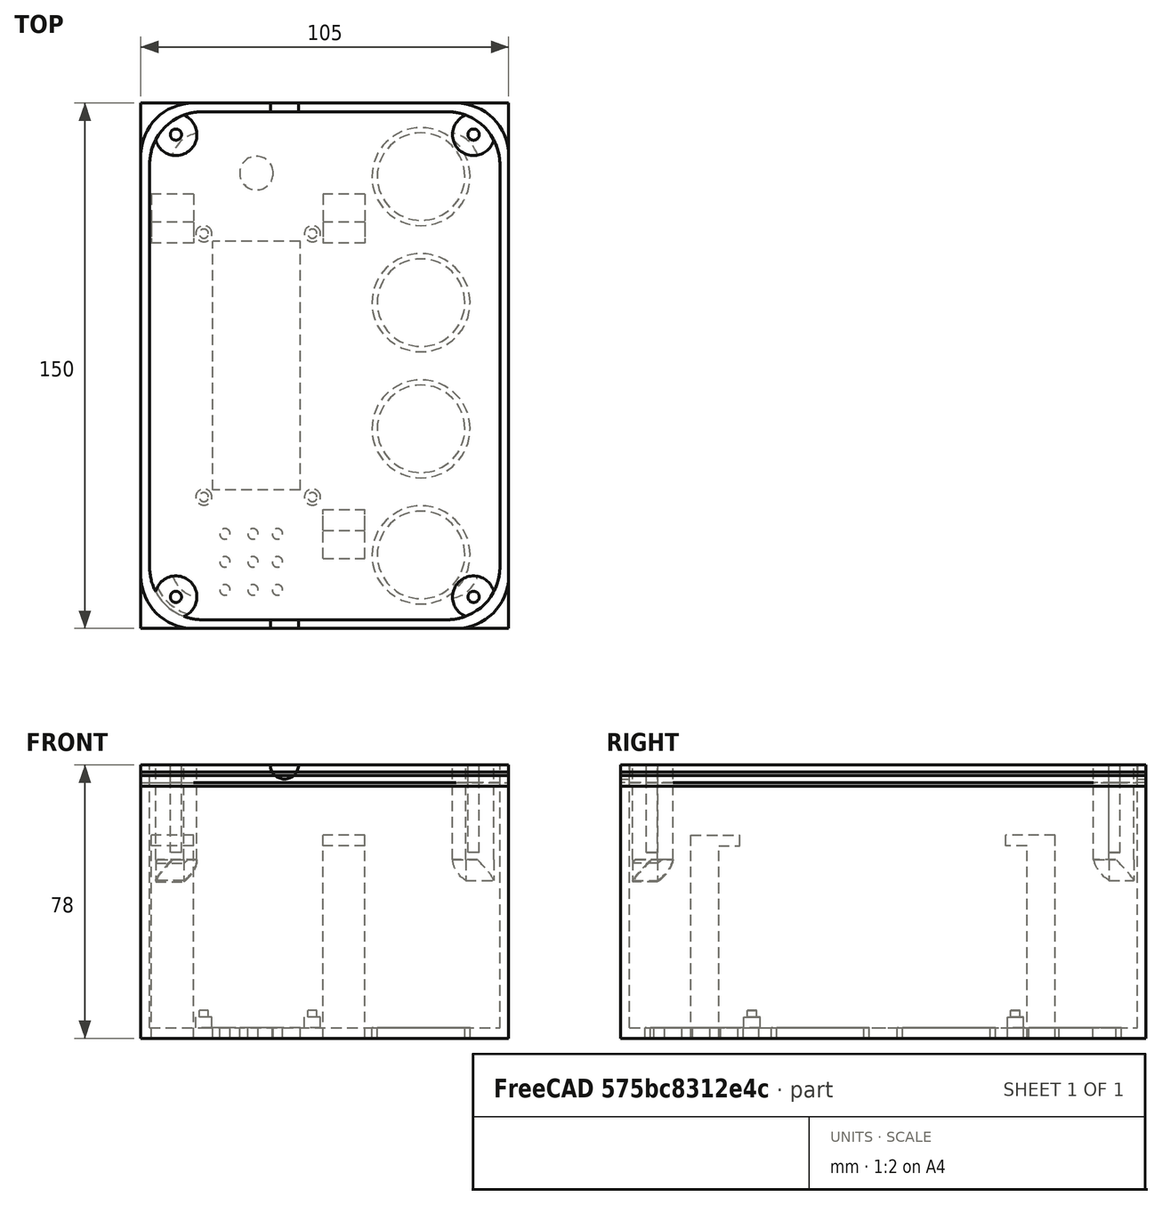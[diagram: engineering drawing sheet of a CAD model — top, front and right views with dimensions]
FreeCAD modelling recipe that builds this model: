
FCSTD DOCUMENT  (FreeCAD 0.16R6706 (Git))
Label: Simon_v2
License: All rights reserved
LicenseURL: http://en.wikipedia.org/wiki/All_rights_reserved
objects: Part::Cylinder×29, Part::Box×13, Part::Cut×13, Part::MultiFuse×11, Part::FeaturePython×6, Part::Fillet×5, Part::Chamfer×5, Mesh::Feature×1, Part::Fuse×1
note: 83 computed .brp shape members not serialized (recipe doc carries the construction recipe); baked Part::Feature solids carry a one-line shape summary decoded from their .brp

FEATURE [Part::Box] Box  label="Cubo"
  Height = 78
  Length = 105
  Width = 150
FEATURE [Part::Box] Box001  label="Cubo001"
  Height = 75
  Length = 100
  Placement = pos=(2.5,2.5,3) rot=(0,0,1;0rad)
  Width = 145
FEATURE [Part::Cut] Cut  label="caja"
  Base = -> Box
  Tool = -> Box001
FEATURE [Part::Cylinder] Cylinder  label="Cilindro"
  Angle = 360
  Height = 10
  Placement = pos=(80,25,0) rot=(0,0,1;0rad)
  Radius = 14
FEATURE [Part::FeaturePython] Array  label="Botones"  # Draft array (typed FeaturePython)
  Angle = 360
  ArrayType = 0
  Axis = (0,0,1)
  Base = -> Cylinder
  Center = (0,0,0)
  Fuse = false
  IntervalAxis = (0,0,0)
  IntervalX = (1,0,0)
  IntervalY = (0,36,0)
  IntervalZ = (0,0,1)
  NumberPolar = 1
  NumberX = 1
  NumberY = 4
  NumberZ = 1
  Placement = pos=(0,-4,-2) rot=(0,0,1;0rad)
FEATURE [Part::Cut] Cut001
  Base = -> Cut
  Tool = -> Array
FEATURE [Part::Box] Box002  label="Cubo002"
  Height = 10
  Length = 25
  Placement = pos=(20.5,39.5,-1) rot=(0,0,1;0rad)
  Width = 71
FEATURE [Part::Cut] Cut002
  Base = -> Cut001
  Tool = -> Box002
FEATURE [Part::Fillet] Fillet
  Base = -> Cut002
  Edges = 4 edges r=15: [Edge25,Edge26,Edge29,Edge30]
FEATURE [Part::Fillet] Fillet001
  Base = -> Fillet
  Edges = 4 edges r=15: [Edge29,Edge30,Edge33,Edge35]
FEATURE [Mesh::Feature] LCD
  Placement = pos=(15.5,35,8) rot=(0.707107,0.707107,0;3.14159rad)
FEATURE [Part::Cylinder] Cylinder001  label="Cilindro001"
  Angle = 360
  Height = 5
  Placement = pos=(18,37.5,3) rot=(0,0,1;0rad)
  Radius = 1.3
FEATURE [Part::FeaturePython] Array001  # Draft array (typed FeaturePython)
  Angle = 360
  ArrayType = 0
  Axis = (0,0,1)
  Base = -> Cylinder001
  Center = (0,0,0)
  Fuse = false
  IntervalAxis = (0,0,0)
  IntervalX = (31,0,0)
  IntervalY = (0,75.2,0)
  IntervalZ = (0,0,1)
  NumberPolar = 1
  NumberX = 2
  NumberY = 2
  NumberZ = 1
FEATURE [Part::Cylinder] Cylinder002  label="Cilindro002"
  Angle = 360
  Height = 3
  Placement = pos=(18,37.5,3) rot=(0,0,1;0rad)
  Radius = 2.3
FEATURE [Part::FeaturePython] Array002  # Draft array (typed FeaturePython)
  Angle = 360
  ArrayType = 0
  Axis = (0,0,1)
  Base = -> Cylinder002
  Center = (0,0,0)
  Fuse = false
  IntervalAxis = (0,0,0)
  IntervalX = (31,0,0)
  IntervalY = (0,75.2,0)
  IntervalZ = (0,0,1)
  NumberPolar = 1
  NumberX = 2
  NumberY = 2
  NumberZ = 1
FEATURE [Part::Fuse] Fusion
  Base = -> Array001
  Tool = -> Array002
FEATURE [Part::MultiFuse] Fusion001
  Shapes = -> [Fillet001,Fusion]
FEATURE [Part::Cylinder] Cylinder003  label="Cilindro003"
  Angle = 360
  Height = 27
  Placement = pos=(10,9,51) rot=(0,0,1;0rad)
  Radius = 6
FEATURE [Part::MultiFuse] Fusion002
  Shapes = -> [Fusion001,Cylinder003]
FEATURE [Part::Chamfer] Chamfer
  Base = -> Fusion002
  Edges = 1 edges r=6.3: [Edge8]
FEATURE [Part::Chamfer] Chamfer001
  Base = -> Fusion002
  Edges = 1 edges r=1: [Edge8]
FEATURE [Part::Cylinder] Cylinder004  label="Cilindro004"
  Angle = 360
  Height = 27
  Placement = pos=(95,9,51) rot=(0,0,1;0rad)
  Radius = 6
FEATURE [Part::Cylinder] Cylinder005  label="Cilindro005"
  Angle = 360
  Height = 27
  Placement = pos=(95,141,51) rot=(0,0,1;0rad)
  Radius = 6
FEATURE [Part::Cylinder] Cylinder007  label="Cilindro007"
  Angle = 360
  Height = 27
  Placement = pos=(10,141,51) rot=(0,0,1;0rad)
  Radius = 6
FEATURE [Part::MultiFuse] Fusion003
  Shapes = -> [Cylinder004,Cylinder005,Cylinder007]
FEATURE [Part::MultiFuse] Fusion004
  Shapes = -> [Chamfer,Fusion003]
FEATURE [Part::Chamfer] Chamfer002
  Base = -> Fusion004
  Edges = 1 edges r=6: [Edge94]
FEATURE [Part::Chamfer] Chamfer003
  Base = -> Chamfer002
  Edges = 1 edges r=6: [Edge96]
FEATURE [Part::Chamfer] Chamfer004
  Base = -> Chamfer003
  Edges = 1 edges r=6: [Edge88]
FEATURE [Part::Cylinder] Cylinder008  label="Cilindro008"
  Angle = 360
  Height = 28
  Placement = pos=(10,141,51) rot=(0,0,1;0rad)
  Radius = 1.6
FEATURE [Part::Cylinder] Cylinder009  label="Cilindro009"
  Angle = 360
  Height = 28
  Placement = pos=(95,9,51) rot=(0,0,1;0rad)
  Radius = 1.6
FEATURE [Part::Cylinder] Cylinder010  label="Cilindro010"
  Angle = 360
  Height = 27
  Placement = pos=(95,141,51) rot=(0,0,1;0rad)
  Radius = 1.6
FEATURE [Part::Cylinder] Cylinder011  label="Cilindro011"
  Angle = 360
  Height = 29
  Placement = pos=(10,9,51) rot=(0,0,1;0rad)
  Radius = 1.6
FEATURE [Part::MultiFuse] Fusion005
  Placement = pos=(0,0,2) rot=(0,0,1;0rad)
  Shapes = -> [Cylinder011,Cylinder008,Cylinder010,Cylinder009]
FEATURE [Part::Cut] Cut003
  Base = -> Chamfer004
  Tool = -> Fusion005
FEATURE [Part::Cylinder] Cylinder012  label="Cilindro012"
  Angle = 360
  Height = 10
  Placement = pos=(80,25,0) rot=(0,0,1;0rad)
  Radius = 14
FEATURE [Part::Box] Box003  label="Cubo003"
  Height = 10
  Length = 25
  Placement = pos=(20.5,39.5,-1) rot=(0,0,1;0rad)
  Width = 71
FEATURE [Part::Box] Box004  label="Cubo004"
  Height = 70
  Length = 100
  Placement = pos=(2.5,2.5,3) rot=(0,0,1;0rad)
  Width = 145
FEATURE [Part::Box] Box005  label="Cubo005"
  Height = 3
  Length = 105
  Width = 150
FEATURE [Part::Cut] Cut004  label="caja001"
  Base = -> Box005
  Tool = -> Box004
FEATURE [Part::FeaturePython] Array003  label="Botones001"  # Draft array (typed FeaturePython)
  Angle = 360
  ArrayType = 0
  Axis = (0,0,1)
  Base = -> Cylinder012
  Center = (0,0,0)
  Fuse = false
  IntervalAxis = (0,0,0)
  IntervalX = (1,0,0)
  IntervalY = (0,36,0)
  IntervalZ = (0,0,1)
  NumberPolar = 1
  NumberX = 1
  NumberY = 4
  NumberZ = 1
  Placement = pos=(0,-4,-2) rot=(0,0,1;0rad)
FEATURE [Part::Cut] Cut005
  Base = -> Cut004
  Tool = -> Array003
FEATURE [Part::Cut] Cut006
  Base = -> Cut005
  Tool = -> Box003
FEATURE [Part::Fillet] Fillet003
  Base = -> Cut006
  Edges = 4 edges r=15: [Edge25,Edge26,Edge29,Edge30]
FEATURE [Part::Fillet] Fillet002
  Base = -> Fillet003
  Edges = 4 edges r=15: [Edge29,Edge30,Edge33,Edge35]
FEATURE [Part::Cut] Cut007  label="caja002"
  Base = -> Box005
  Placement = pos=(0,0,72) rot=(0,0,1;0rad)
  Tool = -> Box004
FEATURE [Part::Box] Box006  label="Cubo006"
  Height = 3
  Length = 105
  Width = 150
FEATURE [Part::Fillet] Fillet004
  Base = -> Box006
  Edges = 4 edges r=15: [Edge1,Edge3,Edge5,Edge7]
  Placement = pos=(0,0,72) rot=(0,0,1;0rad)
FEATURE [Part::Cylinder] Cylinder013  label="Cilindro013"
  Angle = 360
  Height = 22
  Placement = pos=(95,9,51) rot=(0,0,1;0rad)
  Radius = 1.6
FEATURE [Part::Cylinder] Cylinder014  label="Cilindro014"
  Angle = 360
  Height = 22
  Placement = pos=(10,9,51) rot=(0,0,1;0rad)
  Radius = 1.6
FEATURE [Part::Cylinder] Cylinder015  label="Cilindro015"
  Angle = 360
  Height = 22
  Placement = pos=(10,141,51) rot=(0,0,1;0rad)
  Radius = 1.6
FEATURE [Part::Cylinder] Cylinder016  label="Cilindro016"
  Angle = 360
  Height = 22
  Placement = pos=(95,141,51) rot=(0,0,1;0rad)
  Radius = 1.6
FEATURE [Part::MultiFuse] Fusion006
  Placement = pos=(0,0,7) rot=(0,0,1;0rad)
  Shapes = -> [Cylinder014,Cylinder015,Cylinder016,Cylinder013]
FEATURE [Part::Cut] Cut008
  Base = -> Fillet004
  Placement = pos=(0,0,1) rot=(0,0,1;0rad)
  Tool = -> Fusion006
FEATURE [Part::Cylinder] Cylinder017  label="Cilindro017"
  Angle = 360
  Height = 10
  Placement = pos=(24,27,0) rot=(0,0,1;0rad)
  Radius = 1.5
FEATURE [Part::Cylinder] Cylinder018  label="Cilindro018"
  Angle = 360
  Height = 10
  Placement = pos=(24,19,0) rot=(0,0,1;0rad)
  Radius = 1.5
FEATURE [Part::Cylinder] Cylinder019  label="Cilindro019"
  Angle = 360
  Height = 10
  Placement = pos=(24,11,0) rot=(0,0,1;0rad)
  Radius = 1.5
FEATURE [Part::Cylinder] Cylinder020  label="Cilindro020"
  Angle = 360
  Height = 10
  Placement = pos=(32,27,0) rot=(0,0,1;0rad)
  Radius = 1.5
FEATURE [Part::Cylinder] Cylinder021  label="Cilindro021"
  Angle = 360
  Height = 10
  Placement = pos=(32,19,0) rot=(0,0,1;0rad)
  Radius = 1.5
FEATURE [Part::Cylinder] Cylinder022  label="Cilindro022"
  Angle = 360
  Height = 10
  Placement = pos=(32,11,0) rot=(0,0,1;0rad)
  Radius = 1.5
FEATURE [Part::Cylinder] Cylinder023  label="Cilindro023"
  Angle = 360
  Height = 10
  Placement = pos=(39,27,0) rot=(0,0,1;0rad)
  Radius = 1.5
FEATURE [Part::Cylinder] Cylinder024  label="Cilindro024"
  Angle = 360
  Height = 10
  Placement = pos=(39,19,0) rot=(0,0,1;0rad)
  Radius = 1.5
FEATURE [Part::Cylinder] Cylinder025  label="Cilindro025"
  Angle = 360
  Height = 10
  Placement = pos=(39,11,0) rot=(0,0,1;0rad)
  Radius = 1.5
FEATURE [Part::MultiFuse] Fusion007  label="altavoces"
  Shapes = -> [Cylinder017,Cylinder023,Cylinder024,Cylinder018,Cylinder020,Cylinder021,Cylinder025,Cylinder019,Cylinder022]
FEATURE [Part::Cut] Cut009
  Base = -> Cut003
  Tool = -> Fusion007
FEATURE [Part::Cylinder] Cylinder026  label="Cilindro026"
  Angle = 180
  Height = 157
  Placement = pos=(41,-3,78) rot=(-1,0,0;1.5708rad)
  Radius = 4
FEATURE [Part::Cut] Cut010
  Base = -> Cut009
  Tool = -> Cylinder026
FEATURE [Part::Cylinder] Cylinder027  label="Cilindro027"
  Angle = 360
  Height = 10
  Placement = pos=(33,130,-5) rot=(0,0,1;0rad)
  Radius = 4.8
FEATURE [Part::Box] Box007  label="sporte1"
  Height = 55
  Length = 12
  Placement = pos=(47,17,0) rot=(0,0,1;0rad)
  Width = 8
FEATURE [Part::Box] Box008  label="L_soporte1"
  Height = 3
  Length = 12
  Placement = pos=(47,17,55) rot=(0,0,1;0rad)
  Width = 14
FEATURE [Part::Cut] Cut011
  Base = -> Cut010
  Tool = -> Cylinder027
FEATURE [Part::MultiFuse] Fusion008  label="L1"
  Placement = pos=(5,3,0) rot=(0,0,1;0rad)
  Shapes = -> [Box008,Box007]
FEATURE [Part::Box] Box015  label="sporte002"
  Height = 55
  Length = 12
  Placement = pos=(47,17,0) rot=(0,0,1;0rad)
  Width = 8
FEATURE [Part::Box] Box016  label="L_soporte002"
  Height = 3
  Length = 12
  Placement = pos=(47,17,55) rot=(0,0,1;0rad)
  Width = 14
FEATURE [Part::MultiFuse] Fusion009  label="L2"
  Placement = pos=(111,141,0) rot=(0,0,1;3.14159rad)
  Shapes = -> [Box016,Box015]
FEATURE [Part::Box] Box017  label="L_soporte003"
  Height = 3
  Length = 12
  Placement = pos=(47,17,55) rot=(0,0,1;0rad)
  Width = 14
FEATURE [Part::Box] Box018  label="sporte003"
  Height = 55
  Length = 12
  Placement = pos=(47,17,0) rot=(0,0,1;0rad)
  Width = 8
FEATURE [Part::MultiFuse] Fusion010  label="L3"
  Placement = pos=(62,141,0) rot=(0,0,1;3.14159rad)
  Shapes = -> [Box017,Box018]
FEATURE [Part::Cylinder] Cylinder028  label="Cilindro028"
  Angle = 360
  Height = 3
  Placement = pos=(80,25,0) rot=(0,0,1;0rad)
  Radius = 14
FEATURE [Part::FeaturePython] Array004  label="Botones002"  # Draft array (typed FeaturePython)
  Angle = 360
  ArrayType = 0
  Axis = (0,0,1)
  Base = -> Cylinder028
  Center = (0,0,0)
  Fuse = false
  IntervalAxis = (0,0,0)
  IntervalX = (1,0,0)
  IntervalY = (0,36,0)
  IntervalZ = (0,0,1)
  NumberPolar = 1
  NumberX = 1
  NumberY = 4
  NumberZ = 1
  Placement = pos=(0,-4,0) rot=(0,0,1;0rad)
FEATURE [Part::Cylinder] Cylinder029  label="Cilindro029"
  Angle = 360
  Height = 10
  Placement = pos=(80,25,0) rot=(0,0,1;0rad)
  Radius = 12.5
FEATURE [Part::FeaturePython] Array005  label="Botones003"  # Draft array (typed FeaturePython)
  Angle = 360
  ArrayType = 0
  Axis = (0,0,1)
  Base = -> Cylinder029
  Center = (0,0,0)
  Fuse = false
  IntervalAxis = (0,0,0)
  IntervalX = (1,0,0)
  IntervalY = (0,36,0)
  IntervalZ = (0,0,1)
  NumberPolar = 1
  NumberX = 1
  NumberY = 4
  NumberZ = 1
  Placement = pos=(0,-4,-2) rot=(0,0,1;0rad)
FEATURE [Part::MultiFuse] Fusion011
  Shapes = -> [Cut011,Array004]
FEATURE [Part::Cut] Cut012
  Base = -> Fusion011
  Tool = -> Array005
